# Revit family: RN 84233 Optiflex-Flowpress-Übergang
name_source: partatom
category: Rohrformteile
units: mm (PartAtom-declared; Revit-internal decimal feet)

## family parameters
Arbeitsebenenbasiert = Nein
Beim Laden mit Abzugskörper schneiden = Nein
Bemaßung runder Anschluss = Durchmesser verwenden
Gemeinsam genutzt = Nein
Immer vertikal = Ja
Teiletyp = Verbindung

## types (10) — shared parameters
1.010.00.2 Blattnummer der Richtlinie = 29
1.010.00.3 Ausgabedatum (Monat) der Richtlinie = 201308
1.010.00.4 Herstellername = R. Nussbaum AG
1.010.00.5 Revisionsdatum der Datei = 20190521
1.010.00.6 Webadresse des Herstellers = http://www.nussbaum.ch
1.100.00.4 Produktbezeichnung = Versorgung
1.110.00.2 Index = 5
1.110.00.4 Produktbezeichnung = Optiflex
1.960/3L.00.8 Link (URL) = https://www.nussbaum.ch
29.700.00.4 Produktname = Optiflex-Flowpress-Übergang, auf Optipress-Aquaplus, mit Pressmuffe
29.700.00.5 Produktkennung = 2
29.700.00.6 Querschnittsform = 1
29.700.00.7 Nennweitensystem = DN
29.700.00.8 Nenndrucksystem = PN
29.710.02.4 Nenndruck = 10
29.710.02.5 max. zul. Überdruck [hPa] = 1000
29.710.02.7 max. zul. Dauer-Betriebsdruck [hPa] = 1000
29.710.02.9 max. zul. Dauer-Betriebstemperatur [°C] = 70
Connector Visibility = Nein
EnclosingSpace Visibility = Nein
Hersteller = R. Nussbaum AG
URL = https://www.nussbaum.ch

## per-type parameters (varying)
- DN=40x32: 1.800.00.3 TGA-Nummer=01900500000000000000000000000000000000000000000018000000000000000010; 1.800.00.4 Kommentarfeld=84233.30, Optiflex-Flowpress-Übergang, auf Optipress-Aquaplus, mit Pressmuffe, DN=40x32, L=76; 1.810.00.3 Hersteller-Bestellnummer=84233.30; 1.810.00.4 DATANORM-Nummer=84233.30; 1.810.00.6 GTIN-Nummer=7612945744814; 29.710.02.10 Formstück-Gewicht [kg]=0.305; 29.710.02.3 Benennung=Optiflex-Flowpress-Übergang, auf Optipress-Aquaplus, mit Pressmuffe, DN=40x32, L=76; CONNECTOR0_DIAMETER_dX_0r=40 mm; CONNECTOR0_dX_01=26 mm; CONNECTOR0_ref_dX=26 mm; CONNECTOR1_DIAMETER_dX_0r=32 mm; CONNECTOR1_dX_00=50 mm  [stored 0.164042 ft]; CONNECTOR1_dX_01=76 mm; CONNECTOR1_ref_dX=50 mm  [stored 0.164042 ft]; Modell=84233.30; R. Nussbaum AG 84233.21 de Visibility=Nein; R. Nussbaum AG 84233.22 de Visibility=Nein; R. Nussbaum AG 84233.23 de Visibility=Nein; R. Nussbaum AG 84233.24 de Visibility=Nein; R. Nussbaum AG 84233.25 de Visibility=Nein; R. Nussbaum AG 84233.26 de Visibility=Nein; R. Nussbaum AG 84233.27 de Visibility=Nein; R. Nussbaum AG 84233.28 de Visibility=Nein; R. Nussbaum AG 84233.29 de Visibility=Nein; R. Nussbaum AG 84233.30 de Visibility=Ja; Typenkommentare=Optiflex-Flowpress-Übergang DN=40x32
- DN=32: 1.800.00.3 TGA-Nummer=01900500000000000000000000000000000000000000000018000000000000000009; 1.800.00.4 Kommentarfeld=84233.29, Optiflex-Flowpress-Übergang, auf Optipress-Aquaplus, mit Pressmuffe, DN=32, L=70; 1.810.00.3 Hersteller-Bestellnummer=84233.29; 1.810.00.4 DATANORM-Nummer=84233.29; 1.810.00.6 GTIN-Nummer=7612945730770; 29.710.02.10 Formstück-Gewicht [kg]=0.226; 29.710.02.3 Benennung=Optiflex-Flowpress-Übergang, auf Optipress-Aquaplus, mit Pressmuffe, DN=32, L=70; CONNECTOR0_DIAMETER_dX_0r=32 mm; CONNECTOR0_dX_01=26 mm; CONNECTOR0_ref_dX=26 mm; CONNECTOR1_DIAMETER_dX_0r=32 mm; CONNECTOR1_dX_00=44 mm; CONNECTOR1_dX_01=70 mm; CONNECTOR1_ref_dX=44 mm; Modell=84233.29; R. Nussbaum AG 84233.21 de Visibility=Nein; R. Nussbaum AG 84233.22 de Visibility=Nein; R. Nussbaum AG 84233.23 de Visibility=Nein; R. Nussbaum AG 84233.24 de Visibility=Nein; R. Nussbaum AG 84233.25 de Visibility=Nein; R. Nussbaum AG 84233.26 de Visibility=Nein; R. Nussbaum AG 84233.27 de Visibility=Nein; R. Nussbaum AG 84233.28 de Visibility=Nein; R. Nussbaum AG 84233.29 de Visibility=Ja; R. Nussbaum AG 84233.30 de Visibility=Nein; Typenkommentare=Optiflex-Flowpress-Übergang DN=32
- DN=32x25: 1.800.00.3 TGA-Nummer=01900500000000000000000000000000000000000000000018000000000000000008; 1.800.00.4 Kommentarfeld=84233.28, Optiflex-Flowpress-Übergang, auf Optipress-Aquaplus, mit Pressmuffe, DN=32x25, L=71; 1.810.00.3 Hersteller-Bestellnummer=84233.28; 1.810.00.4 DATANORM-Nummer=84233.28; 1.810.00.6 GTIN-Nummer=7612945730763; 29.710.02.10 Formstück-Gewicht [kg]=0.213; 29.710.02.3 Benennung=Optiflex-Flowpress-Übergang, auf Optipress-Aquaplus, mit Pressmuffe, DN=32x25, L=71; CONNECTOR0_DIAMETER_dX_0r=32 mm; CONNECTOR0_dX_01=26 mm; CONNECTOR0_ref_dX=26 mm; CONNECTOR1_DIAMETER_dX_0r=25 mm  [stored 0.082021 ft]; CONNECTOR1_dX_00=47 mm; CONNECTOR1_dX_01=71 mm; CONNECTOR1_ref_dX=47 mm; Modell=84233.28; R. Nussbaum AG 84233.21 de Visibility=Nein; R. Nussbaum AG 84233.22 de Visibility=Nein; R. Nussbaum AG 84233.23 de Visibility=Nein; R. Nussbaum AG 84233.24 de Visibility=Nein; R. Nussbaum AG 84233.25 de Visibility=Nein; R. Nussbaum AG 84233.26 de Visibility=Nein; R. Nussbaum AG 84233.27 de Visibility=Nein; R. Nussbaum AG 84233.28 de Visibility=Ja; R. Nussbaum AG 84233.29 de Visibility=Nein; R. Nussbaum AG 84233.30 de Visibility=Nein; Typenkommentare=Optiflex-Flowpress-Übergang DN=32x25
- DN=25: 1.800.00.3 TGA-Nummer=01900500000000000000000000000000000000000000000018000000000000000007; 1.800.00.4 Kommentarfeld=84233.27, Optiflex-Flowpress-Übergang, auf Optipress-Aquaplus, mit Pressmuffe, DN=25, L=59; 1.810.00.3 Hersteller-Bestellnummer=84233.27; 1.810.00.4 DATANORM-Nummer=84233.27; 1.810.00.5 StLB-Nummer=346.474; 1.810.00.6 GTIN-Nummer=7612945730756; 29.710.02.10 Formstück-Gewicht [kg]=0.133; 29.710.02.3 Benennung=Optiflex-Flowpress-Übergang, auf Optipress-Aquaplus, mit Pressmuffe, DN=25, L=59; CONNECTOR0_DIAMETER_dX_0r=25 mm  [stored 0.082021 ft]; CONNECTOR0_dX_01=20 mm; CONNECTOR0_ref_dX=20 mm; CONNECTOR1_DIAMETER_dX_0r=25 mm  [stored 0.082021 ft]; CONNECTOR1_dX_00=35 mm; CONNECTOR1_dX_01=59 mm; CONNECTOR1_ref_dX=35 mm; Modell=84233.27; R. Nussbaum AG 84233.21 de Visibility=Nein; R. Nussbaum AG 84233.22 de Visibility=Nein; R. Nussbaum AG 84233.23 de Visibility=Nein; R. Nussbaum AG 84233.24 de Visibility=Nein; R. Nussbaum AG 84233.25 de Visibility=Nein; R. Nussbaum AG 84233.26 de Visibility=Nein; R. Nussbaum AG 84233.27 de Visibility=Ja; R. Nussbaum AG 84233.28 de Visibility=Nein; R. Nussbaum AG 84233.29 de Visibility=Nein; R. Nussbaum AG 84233.30 de Visibility=Nein; Typenkommentare=Optiflex-Flowpress-Übergang DN=25
- DN=20: 1.800.00.3 TGA-Nummer=01900500000000000000000000000000000000000000000018000000000000000006; 1.800.00.4 Kommentarfeld=84233.26, Optiflex-Flowpress-Übergang, auf Optipress-Aquaplus, mit Pressmuffe, DN=20, L=59; 1.810.00.3 Hersteller-Bestellnummer=84233.26; 1.810.00.4 DATANORM-Nummer=84233.26; 1.810.00.5 StLB-Nummer=346.473; 1.810.00.6 GTIN-Nummer=7612945730749; 29.710.02.10 Formstück-Gewicht [kg]=0.097; 29.710.02.3 Benennung=Optiflex-Flowpress-Übergang, auf Optipress-Aquaplus, mit Pressmuffe, DN=20, L=59; CONNECTOR0_DIAMETER_dX_0r=20 mm; CONNECTOR0_dX_01=20 mm; CONNECTOR0_ref_dX=20 mm; CONNECTOR1_DIAMETER_dX_0r=20 mm; CONNECTOR1_dX_00=35 mm; CONNECTOR1_dX_01=59 mm; CONNECTOR1_ref_dX=35 mm; Modell=84233.26; R. Nussbaum AG 84233.21 de Visibility=Nein; R. Nussbaum AG 84233.22 de Visibility=Nein; R. Nussbaum AG 84233.23 de Visibility=Nein; R. Nussbaum AG 84233.24 de Visibility=Nein; R. Nussbaum AG 84233.25 de Visibility=Nein; R. Nussbaum AG 84233.26 de Visibility=Ja; R. Nussbaum AG 84233.27 de Visibility=Nein; R. Nussbaum AG 84233.28 de Visibility=Nein; R. Nussbaum AG 84233.29 de Visibility=Nein; R. Nussbaum AG 84233.30 de Visibility=Nein; Typenkommentare=Optiflex-Flowpress-Übergang DN=20
- DN=15x20: 1.800.00.3 TGA-Nummer=01900500000000000000000000000000000000000000000018000000000000000005; 1.800.00.4 Kommentarfeld=84233.25, Optiflex-Flowpress-Übergang, auf Optipress-Aquaplus, mit Pressmuffe, DN=15x20, L=53; 1.810.00.3 Hersteller-Bestellnummer=84233.25; 1.810.00.4 DATANORM-Nummer=84233.25; 1.810.00.5 StLB-Nummer=346.472; 1.810.00.6 GTIN-Nummer=7612945730732; 29.710.02.10 Formstück-Gewicht [kg]=0.067; 29.710.02.3 Benennung=Optiflex-Flowpress-Übergang, auf Optipress-Aquaplus, mit Pressmuffe, DN=15x20, L=53; CONNECTOR0_DIAMETER_dX_0r=15 mm; CONNECTOR0_dX_01=14 mm  [stored 0.0459318 ft]; CONNECTOR0_ref_dX=14 mm  [stored 0.0459318 ft]; CONNECTOR1_DIAMETER_dX_0r=20 mm; CONNECTOR1_dX_00=29 mm  [stored 0.0951444 ft]; CONNECTOR1_dX_01=53 mm; CONNECTOR1_ref_dX=29 mm  [stored 0.0951444 ft]; Modell=84233.25; R. Nussbaum AG 84233.21 de Visibility=Nein; R. Nussbaum AG 84233.22 de Visibility=Nein; R. Nussbaum AG 84233.23 de Visibility=Nein; R. Nussbaum AG 84233.24 de Visibility=Nein; R. Nussbaum AG 84233.25 de Visibility=Ja; R. Nussbaum AG 84233.26 de Visibility=Nein; R. Nussbaum AG 84233.27 de Visibility=Nein; R. Nussbaum AG 84233.28 de Visibility=Nein; R. Nussbaum AG 84233.29 de Visibility=Nein; R. Nussbaum AG 84233.30 de Visibility=Nein; Typenkommentare=Optiflex-Flowpress-Übergang DN=15x20
- DN=15: 1.800.00.3 TGA-Nummer=01900500000000000000000000000000000000000000000018000000000000000004; 1.800.00.4 Kommentarfeld=84233.24, Optiflex-Flowpress-Übergang, auf Optipress-Aquaplus, mit Pressmuffe, DN=15, L=51; 1.810.00.3 Hersteller-Bestellnummer=84233.24; 1.810.00.4 DATANORM-Nummer=84233.24; 1.810.00.5 StLB-Nummer=346.472; 1.810.00.6 GTIN-Nummer=7612945730725; 29.710.02.10 Formstück-Gewicht [kg]=0.054; 29.710.02.3 Benennung=Optiflex-Flowpress-Übergang, auf Optipress-Aquaplus, mit Pressmuffe, DN=15, L=51; CONNECTOR0_DIAMETER_dX_0r=15 mm; CONNECTOR0_dX_01=14 mm  [stored 0.0459318 ft]; CONNECTOR0_ref_dX=14 mm  [stored 0.0459318 ft]; CONNECTOR1_DIAMETER_dX_0r=15 mm; CONNECTOR1_dX_00=29 mm  [stored 0.0951444 ft]; CONNECTOR1_dX_01=51 mm; CONNECTOR1_ref_dX=29 mm  [stored 0.0951444 ft]; Modell=84233.24; R. Nussbaum AG 84233.21 de Visibility=Nein; R. Nussbaum AG 84233.22 de Visibility=Nein; R. Nussbaum AG 84233.23 de Visibility=Nein; R. Nussbaum AG 84233.24 de Visibility=Ja; R. Nussbaum AG 84233.25 de Visibility=Nein; R. Nussbaum AG 84233.26 de Visibility=Nein; R. Nussbaum AG 84233.27 de Visibility=Nein; R. Nussbaum AG 84233.28 de Visibility=Nein; R. Nussbaum AG 84233.29 de Visibility=Nein; R. Nussbaum AG 84233.30 de Visibility=Nein; Typenkommentare=Optiflex-Flowpress-Übergang DN=15
- DN=12: 1.800.00.3 TGA-Nummer=01900500000000000000000000000000000000000000000018000000000000000003; 1.800.00.4 Kommentarfeld=84233.23, Optiflex-Flowpress-Übergang, auf Optipress-Aquaplus, mit Pressmuffe, DN=12, L=50; 1.810.00.3 Hersteller-Bestellnummer=84233.23; 1.810.00.4 DATANORM-Nummer=84233.23; 1.810.00.5 StLB-Nummer=346.472; 1.810.00.6 GTIN-Nummer=7612945730718; 29.710.02.10 Formstück-Gewicht [kg]=0.047; 29.710.02.3 Benennung=Optiflex-Flowpress-Übergang, auf Optipress-Aquaplus, mit Pressmuffe, DN=12, L=50; CONNECTOR0_DIAMETER_dX_0r=15 mm; CONNECTOR0_dX_01=14 mm  [stored 0.0459318 ft]; CONNECTOR0_ref_dX=14 mm  [stored 0.0459318 ft]; CONNECTOR1_DIAMETER_dX_0r=12 mm  [stored 0.0393701 ft]; CONNECTOR1_dX_00=28 mm; CONNECTOR1_dX_01=50 mm  [stored 0.164042 ft]; CONNECTOR1_ref_dX=28 mm; Modell=84233.23; R. Nussbaum AG 84233.21 de Visibility=Nein; R. Nussbaum AG 84233.22 de Visibility=Nein; R. Nussbaum AG 84233.23 de Visibility=Ja; R. Nussbaum AG 84233.24 de Visibility=Nein; R. Nussbaum AG 84233.25 de Visibility=Nein; R. Nussbaum AG 84233.26 de Visibility=Nein; R. Nussbaum AG 84233.27 de Visibility=Nein; R. Nussbaum AG 84233.28 de Visibility=Nein; R. Nussbaum AG 84233.29 de Visibility=Nein; R. Nussbaum AG 84233.30 de Visibility=Nein; Typenkommentare=Optiflex-Flowpress-Übergang DN=12
- DN=15x12: 1.800.00.3 TGA-Nummer=01900500000000000000000000000000000000000000000018000000000000000002; 1.800.00.4 Kommentarfeld=84233.22, Optiflex-Flowpress-Übergang, auf Optipress-Aquaplus, mit Pressmuffe, DN=15x12, L=51; 1.810.00.3 Hersteller-Bestellnummer=84233.22; 1.810.00.4 DATANORM-Nummer=84233.22; 1.810.00.5 StLB-Nummer=346.471; 1.810.00.6 GTIN-Nummer=7612945730701; 29.710.02.10 Formstück-Gewicht [kg]=0.047; 29.710.02.3 Benennung=Optiflex-Flowpress-Übergang, auf Optipress-Aquaplus, mit Pressmuffe, DN=15x12, L=51; CONNECTOR0_DIAMETER_dX_0r=12 mm  [stored 0.0393701 ft]; CONNECTOR0_dX_01=14 mm  [stored 0.0459318 ft]; CONNECTOR0_ref_dX=14 mm  [stored 0.0459318 ft]; CONNECTOR1_DIAMETER_dX_0r=15 mm; CONNECTOR1_dX_00=29 mm  [stored 0.0951444 ft]; CONNECTOR1_dX_01=51 mm; CONNECTOR1_ref_dX=29 mm  [stored 0.0951444 ft]; Modell=84233.22; R. Nussbaum AG 84233.21 de Visibility=Nein; R. Nussbaum AG 84233.22 de Visibility=Ja; R. Nussbaum AG 84233.23 de Visibility=Nein; R. Nussbaum AG 84233.24 de Visibility=Nein; R. Nussbaum AG 84233.25 de Visibility=Nein; R. Nussbaum AG 84233.26 de Visibility=Nein; R. Nussbaum AG 84233.27 de Visibility=Nein; R. Nussbaum AG 84233.28 de Visibility=Nein; R. Nussbaum AG 84233.29 de Visibility=Nein; R. Nussbaum AG 84233.30 de Visibility=Nein; Typenkommentare=Optiflex-Flowpress-Übergang DN=15x12
- DN=15x1: 1.800.00.3 TGA-Nummer=01900500000000000000000000000000000000000000000018000000000000000001; 1.800.00.4 Kommentarfeld=84233.21, Optiflex-Flowpress-Übergang, auf Optipress-Aquaplus, mit Pressmuffe, DN=15x12, L=50; 1.810.00.3 Hersteller-Bestellnummer=84233.21; 1.810.00.4 DATANORM-Nummer=84233.21; 1.810.00.5 StLB-Nummer=346.471; 1.810.00.6 GTIN-Nummer=7612945730695; 29.710.02.10 Formstück-Gewicht [kg]=0.042; 29.710.02.3 Benennung=Optiflex-Flowpress-Übergang, auf Optipress-Aquaplus, mit Pressmuffe, DN=15x12, L=50; CONNECTOR0_DIAMETER_dX_0r=12 mm  [stored 0.0393701 ft]; CONNECTOR0_dX_01=14 mm  [stored 0.0459318 ft]; CONNECTOR0_ref_dX=14 mm  [stored 0.0459318 ft]; CONNECTOR1_DIAMETER_dX_0r=12 mm  [stored 0.0393701 ft]; CONNECTOR1_dX_00=28 mm; CONNECTOR1_dX_01=50 mm  [stored 0.164042 ft]; CONNECTOR1_ref_dX=28 mm; Modell=84233.21; R. Nussbaum AG 84233.21 de Visibility=Ja; R. Nussbaum AG 84233.22 de Visibility=Nein; R. Nussbaum AG 84233.23 de Visibility=Nein; R. Nussbaum AG 84233.24 de Visibility=Nein; R. Nussbaum AG 84233.25 de Visibility=Nein; R. Nussbaum AG 84233.26 de Visibility=Nein; R. Nussbaum AG 84233.27 de Visibility=Nein; R. Nussbaum AG 84233.28 de Visibility=Nein; R. Nussbaum AG 84233.29 de Visibility=Nein; R. Nussbaum AG 84233.30 de Visibility=Nein; Typenkommentare=Optiflex-Flowpress-Übergang DN=15x12

note: [stored X ft] marks values corroborated as IEEE doubles in the binary element streams (Revit-internal decimal feet)

## geometry (parser evidence)
native form markers: Sweep x1
no freeform markers — native parametric forms only
